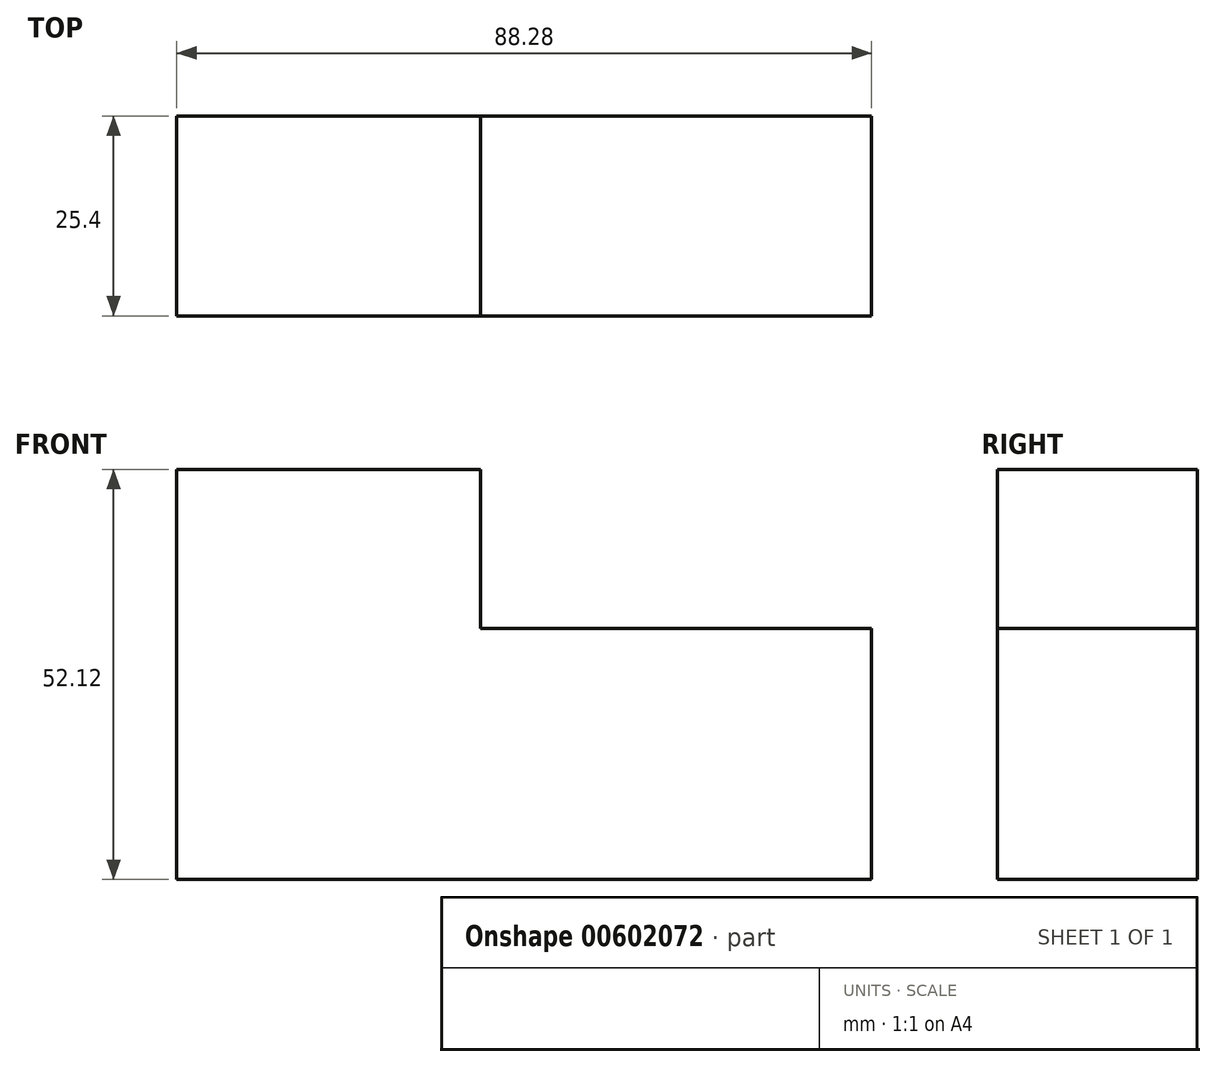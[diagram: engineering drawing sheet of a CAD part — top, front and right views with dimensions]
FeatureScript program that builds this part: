
annotation { "Feature Type Name" : "Feature", "Feature Type Description" : "" }
export const myFeature = defineFeature(function(context is Context, id is Id, definition is map)
    precondition{}
    {
        {
            var Q0;
            Q0=qCreatedBy(makeId("Front.planeOp"),FACE);
            var sketch = newSketch(context, id + "F0", { "sketchPlane" : qUnion([Q0])});
            skLineSegment(sketch, "E0", {"start": v(-68.56, 64.27) * mm, "end": v(-68.56, 12.15) * mm});
            skLineSegment(sketch, "E1", {"start": v(-68.56, 64.27) * mm, "end": v(-29.94, 64.27) * mm});
            skLineSegment(sketch, "E2", {"start": v(-29.94, 64.27) * mm, "end": v(-29.94, 44.04) * mm});
            skLineSegment(sketch, "E3", {"start": v(-29.94, 44.04) * mm, "end": v(19.72, 44.04) * mm});
            skLineSegment(sketch, "E4", {"start": v(19.72, 44.04) * mm, "end": v(19.72, 12.15) * mm});
            skLineSegment(sketch, "E5", {"start": v(19.72, 12.15) * mm, "end": v(-68.56, 12.15) * mm});
            skSolve(sketch);
        }
        {
            var Q0;
            Q0 = qSketchRegion(id + "F0", true);
            extrude(context, id + "F1", {"entities" : qUnion([Q0]), "depth" : 25.4 * mm, "offsetDistance" : 25.4 * mm});
        }
    });
